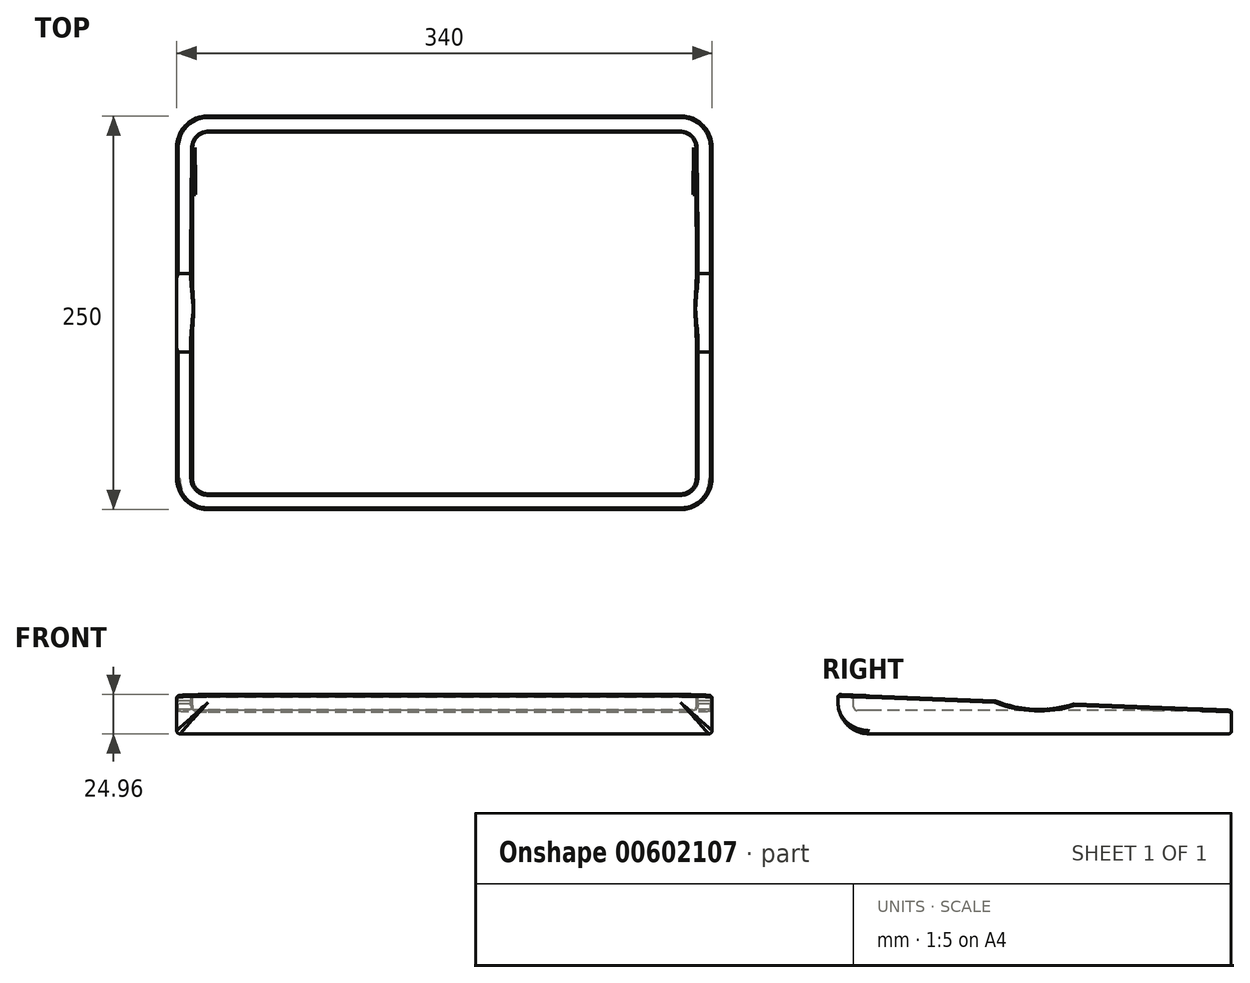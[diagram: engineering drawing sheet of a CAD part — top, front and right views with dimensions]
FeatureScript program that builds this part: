
annotation { "Feature Type Name" : "Feature", "Feature Type Description" : "" }
export const myFeature = defineFeature(function(context is Context, id is Id, definition is map)
    precondition{}
    {
        {
            var Q0;
            Q0=qCreatedBy(makeId("Top.planeOp"),FACE);
            var sketch = newSketch(context, id + "F0", { "sketchPlane" : qUnion([Q0])});
            skLineSegment(sketch, "E0", {"start": v(-141.04, 49.24) * mm, "end": v(198.96, 49.24) * mm});
            skLineSegment(sketch, "E1", {"start": v(198.96, 49.24) * mm, "end": v(198.96, -200.76) * mm});
            skLineSegment(sketch, "E2", {"start": v(-141.04, 49.24) * mm, "end": v(-141.04, -200.76) * mm});
            skLineSegment(sketch, "E3", {"start": v(-141.04, -200.76) * mm, "end": v(198.96, -200.76) * mm});
            skSolve(sketch);
        }
        {
            var Q0;
            Q0=makeQuery(id+"F0.imprint","IMPRINT",FACE,{"disambiguationData":[TD([[makeQuery(id+"F0.imprint","IMPRINT",EDGE,{"derivedFrom":sQuery(id+"F0.wireOp",EDGE,"E0")}),-1.0]])]});
            extrude(context, id + "F1", {"entities" : qUnion([Q0]), "depth" : 25 * mm, "offsetDistance" : 25 * mm});
        }
        {
            var Q0;
            Q0=makeQuery(id+"F1.opExtrude","CAP_FACE",FACE,{"disambiguationData":[OSD([sQuery(id+"F0.wireOp",EDGE,"E0"),sQuery(id+"F0.wireOp",EDGE,"E1"),sQuery(id+"F0.wireOp",EDGE,"E2"),sQuery(id+"F0.wireOp",EDGE,"E3")])],"isStart":false});
            var sketch = newSketch(context, id + "F2", { "sketchPlane" : qUnion([Q0])});
            skLineSegment(sketch, "E4.0", {"start": v(-131.04, 39.24) * mm, "end": v(188.96, 39.24) * mm});
            skLineSegment(sketch, "E4.1", {"start": v(-131.04, 39.24) * mm, "end": v(-131.04, -190.76) * mm});
            skLineSegment(sketch, "E4.2", {"start": v(-131.04, -190.76) * mm, "end": v(188.96, -190.76) * mm});
            skLineSegment(sketch, "E4.3", {"start": v(188.96, 39.24) * mm, "end": v(188.96, -190.76) * mm});
            skSolve(sketch);
        }
        {
            var Q0;
            Q0=makeQuery(id+"F2.imprint","IMPRINT",FACE,{"disambiguationData":[TD([[makeQuery(id+"F2.imprint","IMPRINT",EDGE,{"derivedFrom":sQuery(id+"F2.wireOp",EDGE,"E4.0")}),-1.0]])]});
            extrude(context, id + "F3", {"entities" : qUnion([Q0]), "operationType" : NewBodyOperationType.REMOVE, "oppositeDirection" : true, "depth" : 10 * mm, "offsetDistance" : 25 * mm});
        }
        {
            var Q0;
            Q0=makeQuery(id+"F1.opExtrude","SWEPT_FACE",FACE,{"disambiguationData":[OSD([sQuery(id+"F0.wireOp",EDGE,"E2")])]});
            var sketch = newSketch(context, id + "F4", { "sketchPlane" : qUnion([Q0])});
            skLineSegment(sketch, "E5", {"start": v(-49.24, 25) * mm, "end": v(-63.86, 25) * mm});
            skLineSegment(sketch, "E6", {"start": v(-63.86, 25) * mm, "end": v(-63.86, 15) * mm});
            skLineSegment(sketch, "E7", {"start": v(-63.86, 15) * mm, "end": v(-49.24, 15) * mm});
            skLineSegment(sketch, "E8", {"start": v(-49.24, 15) * mm, "end": v(200.76, 25) * mm});
            skSolve(sketch);
        }
        {
            var Q0;
            {var subQ0=sQuery(id+"F4.wireOp",EDGE,"E8");Q0=makeQuery(id+"F4.imprint","IMPRINT",FACE,{"disambiguationData":[TD([[makeQuery(id+"F4.imprint","IMPRINT",EDGE,{"derivedFrom":subQ0}),1.0]])]});}
            extrude(context, id + "F5", {"entities" : qUnion([Q0]), "operationType" : NewBodyOperationType.REMOVE, "oppositeDirection" : true, "depth" : 412.16 * mm, "offsetDistance" : 25 * mm});
        }
        {
            var Q0;
            Q0=makeQuery(id+"F3.boolean.opBoolean","COPY",EDGE,{"derivedFrom":makeQuery(id+"F3.opExtrude","SWEPT_EDGE",EDGE,{"disambiguationData":[OSD([sQuery(id+"F2.wireOp",EDGE,"E4.2"),sQuery(id+"F2.wireOp",EDGE,"E4.3")])]})});
            fillet(context, id + "F6", {"entities" : qUnion([Q0]), "radius" : 10 * mm, "tangentPropagation" : true, "allowEdgeOverflow" : false});
        }
        {
            var Q0;
            Q0=makeQuery(id+"F3.boolean.opBoolean","COPY",EDGE,{"derivedFrom":makeQuery(id+"F3.opExtrude","SWEPT_EDGE",EDGE,{"disambiguationData":[OSD([sQuery(id+"F2.wireOp",EDGE,"E4.1"),sQuery(id+"F2.wireOp",EDGE,"E4.2")])]})});
            fillet(context, id + "F7", {"entities" : qUnion([Q0]), "radius" : 10 * mm, "tangentPropagation" : true, "allowEdgeOverflow" : false});
        }
        {
            var Q0;
            Q0=makeQuery(id+"F1.opExtrude","SWEPT_EDGE",EDGE,{"disambiguationData":[OSD([sQuery(id+"F0.wireOp",EDGE,"E2"),sQuery(id+"F0.wireOp",EDGE,"E3")])]});
            fillet(context, id + "F8", {"entities" : qUnion([Q0]), "radius" : 20 * mm, "tangentPropagation" : true, "allowEdgeOverflow" : false});
        }
        {
            var Q0;
            Q0=makeQuery(id+"F1.opExtrude","SWEPT_EDGE",EDGE,{"disambiguationData":[OSD([sQuery(id+"F0.wireOp",EDGE,"E1"),sQuery(id+"F0.wireOp",EDGE,"E3")])]});
            fillet(context, id + "F9", {"entities" : qUnion([Q0]), "radius" : 20 * mm, "tangentPropagation" : true, "allowEdgeOverflow" : false});
        }
        {
            var Q0;
            Q0=makeQuery(id+"F1.opExtrude","CAP_EDGE",EDGE,{"disambiguationData":[OSD([sQuery(id+"F0.wireOp",EDGE,"E3")])],"isStart":true});
            fillet(context, id + "F10", {"entities" : qUnion([Q0]), "radius" : 20 * mm, "allowEdgeOverflow" : false});
        }
        {
            var Q0;
            Q0=makeQuery(id+"F1.opExtrude","SWEPT_EDGE",EDGE,{"disambiguationData":[OSD([sQuery(id+"F0.wireOp",EDGE,"E0"),sQuery(id+"F0.wireOp",EDGE,"E2")])]});
            var Q1;
            Q1=makeQuery(id+"F1.opExtrude","SWEPT_EDGE",EDGE,{"disambiguationData":[OSD([sQuery(id+"F0.wireOp",EDGE,"E0"),sQuery(id+"F0.wireOp",EDGE,"E1")])]});
            fillet(context, id + "F11", {"entities" : qUnion([Q0, Q1]), "radius" : 20 * mm, "tangentPropagation" : true, "allowEdgeOverflow" : false});
        }
        {
            var Q0;
            Q0=makeQuery(id+"F3.boolean.opBoolean","COPY",EDGE,{"derivedFrom":makeQuery(id+"F3.opExtrude","SWEPT_EDGE",EDGE,{"disambiguationData":[OSD([sQuery(id+"F2.wireOp",EDGE,"E4.0"),sQuery(id+"F2.wireOp",EDGE,"E4.3")])]})});
            fillet(context, id + "F12", {"entities" : qUnion([Q0]), "radius" : 10 * mm, "tangentPropagation" : true, "allowEdgeOverflow" : false});
        }
        {
            var Q0;
            Q0=makeQuery(id+"F3.boolean.opBoolean","COPY",EDGE,{"derivedFrom":makeQuery(id+"F3.opExtrude","SWEPT_EDGE",EDGE,{"disambiguationData":[OSD([sQuery(id+"F2.wireOp",EDGE,"E4.0"),sQuery(id+"F2.wireOp",EDGE,"E4.1")])]})});
            fillet(context, id + "F13", {"entities" : qUnion([Q0]), "radius" : 10 * mm, "tangentPropagation" : true, "allowEdgeOverflow" : false});
        }
        {
            var Q0;
            Q0=makeQuery(id+"F3.boolean.opBoolean","COPY",EDGE,{"derivedFrom":makeQuery(id+"F3.opExtrude","CAP_EDGE",EDGE,{"disambiguationData":[OSD([sQuery(id+"F2.wireOp",EDGE,"E4.2")])],"isStart":false})});
            fillet(context, id + "F14", {"entities" : qUnion([Q0]), "radius" : 2 * mm, "tangentPropagation" : true, "allowEdgeOverflow" : false});
        }
        {
            var Q0;
            Q0=makeQuery(id+"F1.opExtrude","CAP_EDGE",EDGE,{"disambiguationData":[OSD([sQuery(id+"F0.wireOp",EDGE,"E1")])],"isStart":true});
            fillet(context, id + "F15", {"entities" : qUnion([Q0]), "radius" : 2 * mm, "tangentPropagation" : true, "allowEdgeOverflow" : false});
        }
        {
            var Q0;
            Q0=makeQuery(id+"F1.opExtrude","SWEPT_FACE",FACE,{"disambiguationData":[OSD([sQuery(id+"F0.wireOp",EDGE,"E2")])]});
            var sketch = newSketch(context, id + "F16", { "sketchPlane" : qUnion([Q0])});
            skLineSegment(sketch, "E9", {"start": v(75.76, 20) * mm, "end": v(100.76, 21) * mm});
            skLineSegment(sketch, "E10", {"start": v(75.76, 20) * mm, "end": v(50.76, 19) * mm});
            skArc(sketch, "E11", {"start": v(50.76, 19) * mm, "mid": v(75.94, 15.56) * mm, "end": v(100.76, 21) * mm});
            skPoint(sketch, "E12.end.orphan", {"position": v(72.56, 15.5) * mm});
            skSolve(sketch);
        }
        {
            var Q0;
            Q0=makeQuery(id+"F16.imprint","IMPRINT",FACE,{"disambiguationData":[TD([[makeQuery(id+"F16.imprint","IMPRINT",EDGE,{"derivedFrom":sQuery(id+"F16.wireOp",EDGE,"E9")}),-1.0]])]});
            extrude(context, id + "F17", {"entities" : qUnion([Q0]), "operationType" : NewBodyOperationType.REMOVE, "oppositeDirection" : true, "depth" : 386.4 * mm, "offsetDistance" : 25 * mm});
        }
        {
            var Q0;
            {var subQ0=sQuery(id+"F0.wireOp",EDGE,"E1");var subQ1=makeQuery(id+"F1.opExtrude","SWEPT_FACE",FACE,{"disambiguationData":[OSD([subQ0])]});var subQ2=makeQuery(id+"F5.opExtrude","SWEPT_FACE",FACE,{"disambiguationData":[OSD([sQuery(id+"F4.wireOp",EDGE,"E8")])]});Q0=makeQuery(id+"F17.boolean.opBoolean","SPLIT",EDGE,{"disambiguationData":[TD([makeQuery(id+"F11.opFillet","BLEND_FACE",FACE,{"disambiguationData":[OSD([sQuery(id+"F0.wireOp",EDGE,"E0"),subQ0])]})])],"derivedFrom":makeQuery(id+"F5.boolean.opBoolean","INTERSECT",EDGE,{"derivedFrom":[subQ1,subQ2]})});}
            var Q1;
            Q1=makeQuery(id+"F17.boolean.opBoolean","INTERSECT",EDGE,{"derivedFrom":[makeQuery(id+"F1.opExtrude","SWEPT_FACE",FACE,{"disambiguationData":[OSD([sQuery(id+"F0.wireOp",EDGE,"E1")])]}),makeQuery(id+"F17.opExtrude","SWEPT_FACE",FACE,{"disambiguationData":[OSD([sQuery(id+"F16.wireOp",EDGE,"E11")])]})]});
            var Q2;
            {var subQ0=sQuery(id+"F0.wireOp",EDGE,"E1");var subQ1=makeQuery(id+"F1.opExtrude","SWEPT_FACE",FACE,{"disambiguationData":[OSD([subQ0])]});var subQ2=makeQuery(id+"F5.opExtrude","SWEPT_FACE",FACE,{"disambiguationData":[OSD([sQuery(id+"F4.wireOp",EDGE,"E8")])]});Q2=makeQuery(id+"F17.boolean.opBoolean","SPLIT",EDGE,{"disambiguationData":[TD([makeQuery(id+"F9.opFillet","BLEND_FACE",FACE,{"disambiguationData":[OSD([subQ0,sQuery(id+"F0.wireOp",EDGE,"E3")])]})])],"derivedFrom":makeQuery(id+"F5.boolean.opBoolean","INTERSECT",EDGE,{"derivedFrom":[subQ1,subQ2]})});}
            var Q3;
            Q3=makeQuery(id+"F17.boolean.opBoolean","COPY",EDGE,{"derivedFrom":makeQuery(id+"F17.opExtrude","CAP_EDGE",EDGE,{"disambiguationData":[OSD([sQuery(id+"F16.wireOp",EDGE,"E11")])],"isStart":true})});
            chamfer(context, id + "F18", {"entities" : qUnion([Q0, Q1, Q2, Q3]), "width" : 1 * mm, "tangentPropagation" : true});
        }
        {
            var Q0;
            {var subQ0=sQuery(id+"F2.wireOp",EDGE,"E4.1");var subQ1=makeQuery(id+"F3.boolean.opBoolean","COPY",FACE,{"derivedFrom":makeQuery(id+"F3.opExtrude","SWEPT_FACE",FACE,{"disambiguationData":[OSD([subQ0])]})});var subQ2=makeQuery(id+"F5.opExtrude","SWEPT_FACE",FACE,{"disambiguationData":[OSD([sQuery(id+"F4.wireOp",EDGE,"E8")])]});Q0=makeQuery(id+"F17.boolean.opBoolean","SPLIT",EDGE,{"disambiguationData":[TD([makeQuery(id+"F7.opFillet","BLEND_FACE",FACE,{"disambiguationData":[OSD([subQ0,sQuery(id+"F2.wireOp",EDGE,"E4.2")])]})])],"derivedFrom":makeQuery(id+"F5.boolean.opBoolean","INTERSECT",EDGE,{"derivedFrom":[subQ1,subQ2]})});}
            var Q1;
            Q1=makeQuery(id+"F17.boolean.opBoolean","INTERSECT",EDGE,{"disambiguationData":[OD(1.0)],"derivedFrom":[makeQuery(id+"F3.boolean.opBoolean","COPY",FACE,{"derivedFrom":makeQuery(id+"F3.opExtrude","SWEPT_FACE",FACE,{"disambiguationData":[OSD([sQuery(id+"F2.wireOp",EDGE,"E4.1")])]})}),makeQuery(id+"F17.opExtrude","SWEPT_FACE",FACE,{"disambiguationData":[OSD([sQuery(id+"F16.wireOp",EDGE,"E11")])]})]});
            var Q2;
            {var subQ0=sQuery(id+"F2.wireOp",EDGE,"E4.1");var subQ1=makeQuery(id+"F5.opExtrude","SWEPT_FACE",FACE,{"disambiguationData":[OSD([sQuery(id+"F4.wireOp",EDGE,"E8")])]});var subQ2=makeQuery(id+"F3.boolean.opBoolean","COPY",FACE,{"derivedFrom":makeQuery(id+"F3.opExtrude","SWEPT_FACE",FACE,{"disambiguationData":[OSD([subQ0])]})});Q2=makeQuery(id+"F17.boolean.opBoolean","SPLIT",EDGE,{"disambiguationData":[TD([makeQuery(id+"F14.opFillet","BLEND_FACE",FACE,{"disambiguationData":[OSD([subQ0]),OD(0.0)]})])],"derivedFrom":makeQuery(id+"F5.boolean.opBoolean","INTERSECT",EDGE,{"derivedFrom":[subQ2,subQ1]})});}
            var Q3;
            Q3=makeQuery(id+"F17.boolean.opBoolean","INTERSECT",EDGE,{"disambiguationData":[OD(1.0)],"derivedFrom":[makeQuery(id+"F3.boolean.opBoolean","COPY",FACE,{"derivedFrom":makeQuery(id+"F3.opExtrude","SWEPT_FACE",FACE,{"disambiguationData":[OSD([sQuery(id+"F2.wireOp",EDGE,"E4.3")])]})}),makeQuery(id+"F17.opExtrude","SWEPT_FACE",FACE,{"disambiguationData":[OSD([sQuery(id+"F16.wireOp",EDGE,"E11")])]})]});
            chamfer(context, id + "F19", {"entities" : qUnion([Q0, Q1, Q2, Q3]), "width" : 1 * mm, "tangentPropagation" : true});
        }
    });
